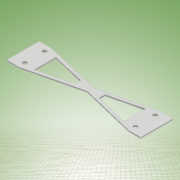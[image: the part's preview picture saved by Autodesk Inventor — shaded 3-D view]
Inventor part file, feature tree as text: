
AUTODESK INVENTOR PART (.ipt)
format: ipt  version: 2017 (Build 210142000, 142)  size: 140,288 bytes
history: native  units: mm
features: extrude x1, sketch x1
ambient origin geometry x8: Origin, YZ Plane, XZ Plane, XY Plane, X Axis, Y Axis, Z Axis, Center Point
bodies: Solid1 (feature_tree)
feature tree (2):
  extrude  "Extrusion1"  Depth=1.0mm
  sketch  "Sketch1"  dims[d0=105.0mm d1=15.4mm d3=5.0mm d4=9.077mm d5=3.0mm d6=3.0mm d7=1.0mm d8=0.0mm]
